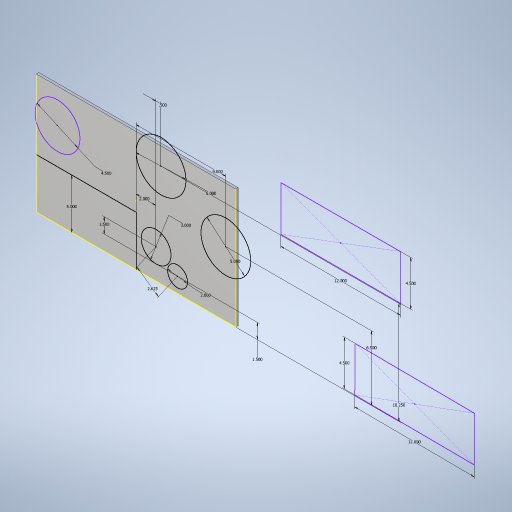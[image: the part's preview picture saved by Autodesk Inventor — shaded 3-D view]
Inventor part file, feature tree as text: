
AUTODESK INVENTOR PART (.ipt)
format: ipt  version: 2023.4 (Build 274418000, 418)  size: 274,944 bytes
history: native  units: in
note: dims shown in document units (in); Inventor stores cm internally (conversion verified against a paired STEP export)
features: sketch x2, extrude x1
ambient origin geometry x8: Origin, YZ Plane, XZ Plane, XY Plane, X Axis, Y Axis, Z Axis, Center Point
bodies: Solid1 (feature_tree)
feature tree (3):
  extrude  "Extrusion1"  Depth=12.0in
  sketch  "Sketch2"  dims[d2=0.25in d3=0.0in d4=5.0in d6=2.0in d7=5.0in d9=12.0in d10=4.5in d11=1.5in d12=6.5in d14=12.0in d15=4.5in d16=4.5in d17=3.0in d18=1.5in d19=2.625in d20=5.0in d21=10.25in d22=2.0in d23=9.0in d24=0.5in]
  sketch  "Sketch1"  dims[d0=20.0in d1=12.0in]
